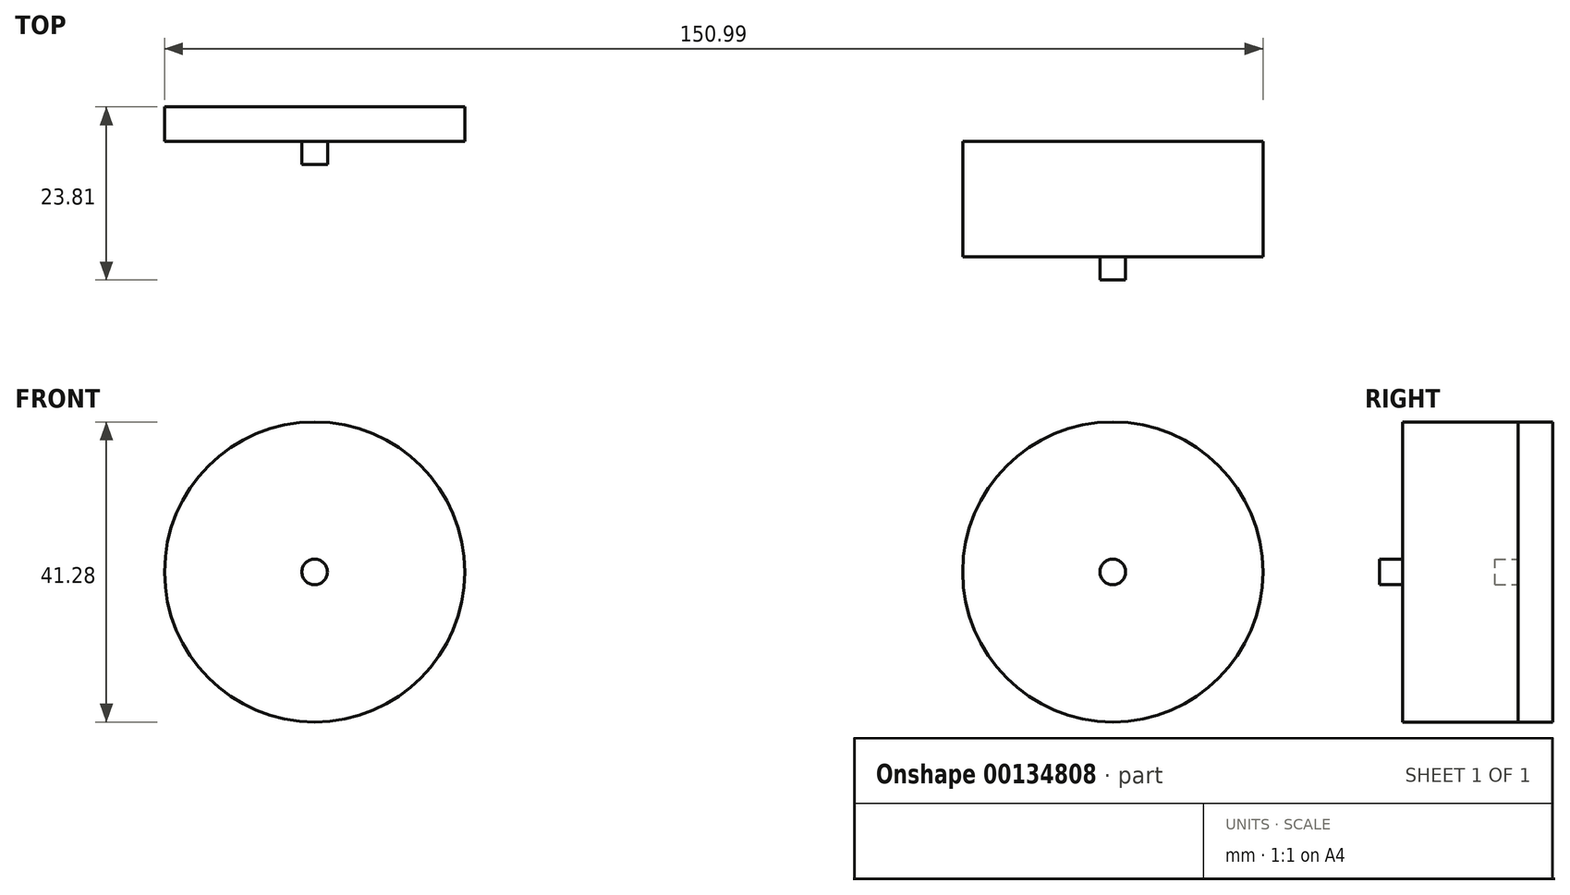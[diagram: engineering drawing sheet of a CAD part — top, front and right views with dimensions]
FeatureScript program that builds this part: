
annotation { "Feature Type Name" : "Feature", "Feature Type Description" : "" }
export const myFeature = defineFeature(function(context is Context, id is Id, definition is map)
    precondition{}
    {
        {
            var Q0;
            Q0=qCreatedBy(makeId("Front.planeOp"),FACE);
            var sketch = newSketch(context, id + "F0", { "sketchPlane" : qUnion([Q0])});
            skCircle(sketch, "E0", {"center": v(-61.98, 0) * mm, "radius": 20.64 * mm});
            skSolve(sketch);
        }
        {
            var Q0;
            Q0 = qSketchRegion(id + "F0", true);
            extrude(context, id + "F1", {"entities" : qUnion([Q0]), "oppositeDirection" : true, "depth" : 4.76 * mm});
        }
        {
            var Q0;
            Q0=makeQuery(id+"F1.opExtrude","CAP_FACE",FACE,{"disambiguationData":[OSD([sQuery(id+"F0.wireOp",EDGE,"E0")])],"isStart":true});
            var sketch = newSketch(context, id + "F2", { "sketchPlane" : qUnion([Q0])});
            skCircle(sketch, "E1", {"center": v(-61.98, 0) * mm, "radius": 1.76 * mm});
            skSolve(sketch);
        }
        {
            var Q0;
            Q0=makeQuery(id+"F2.imprint","IMPRINT",FACE,{"disambiguationData":[TD([[makeQuery(id+"F2.imprint","IMPRINT",EDGE,{"derivedFrom":sQuery(id+"F2.wireOp",EDGE,"E1")}),1.0]])]});
            extrude(context, id + "F3", {"entities" : qUnion([Q0]), "operationType" : NewBodyOperationType.ADD, "depth" : 3.17 * mm});
        }
        {
            var Q0;
            Q0=qCreatedBy(makeId("Front.planeOp"),FACE);
            var sketch = newSketch(context, id + "F4", { "sketchPlane" : qUnion([Q0])});
            skCircle(sketch, "E2", {"center": v(47.74, 0) * mm, "radius": 20.64 * mm});
            skSolve(sketch);
        }
        {
            var Q0;
            Q0=qCreatedBy(makeId("Front.planeOp"),FACE);
            var sketch = newSketch(context, id + "F5", { "sketchPlane" : qUnion([Q0])});
            skCircle(sketch, "E3", {"center": v(47.74, 0) * mm, "radius": 1.76 * mm});
            skSolve(sketch);
        }
        {
            var Q0;
            Q0 = qSketchRegion(id + "F4", true);
            extrude(context, id + "F6", {"entities" : qUnion([Q0]), "depth" : 15.88 * mm});
        }
        {
            var Q0;
            Q0 = qSketchRegion(id + "F5", true);
            extrude(context, id + "F7", {"entities" : qUnion([Q0]), "operationType" : NewBodyOperationType.ADD, "depth" : 19.05 * mm});
        }
    });
